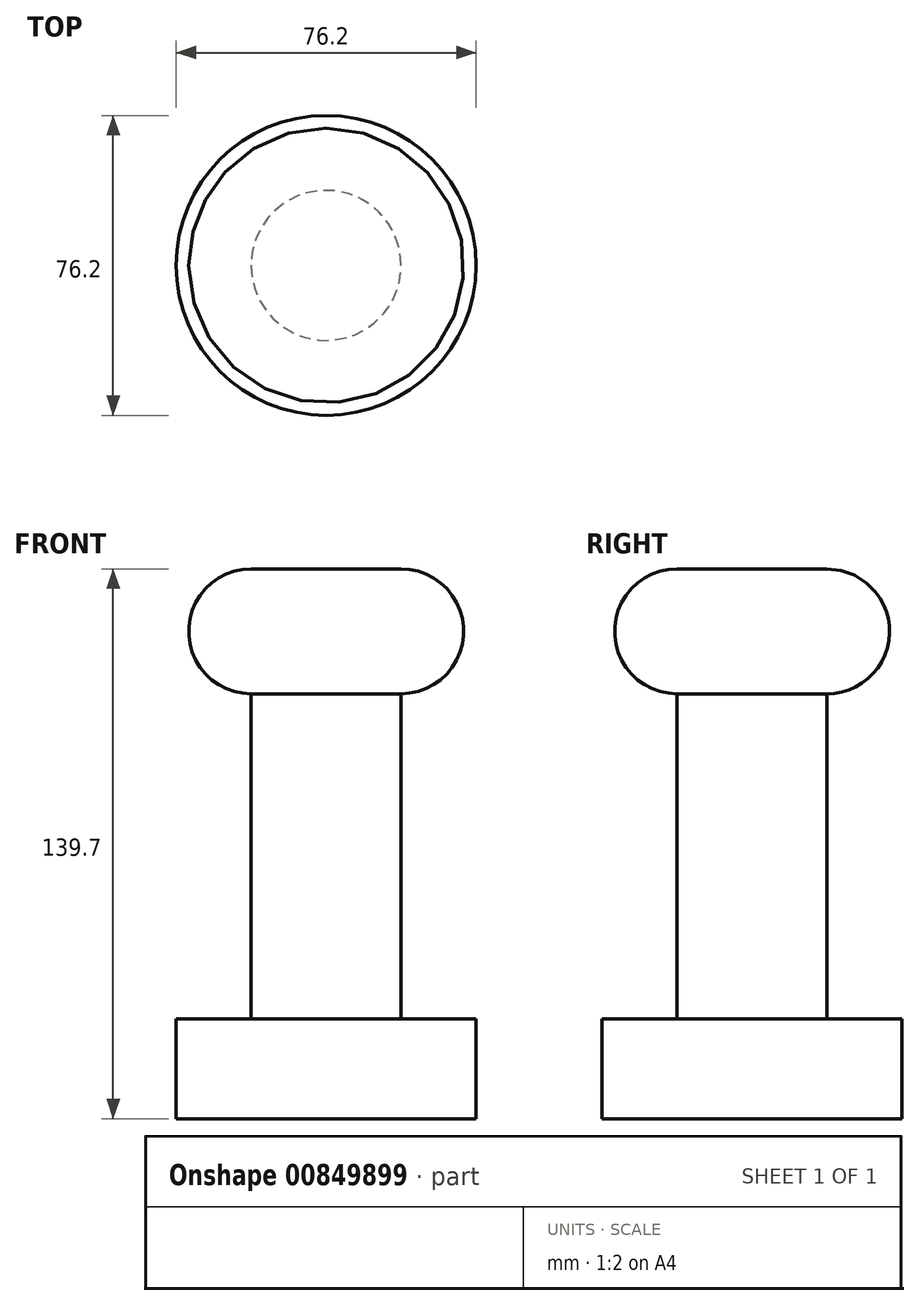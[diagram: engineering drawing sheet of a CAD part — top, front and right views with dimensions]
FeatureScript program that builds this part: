
annotation { "Feature Type Name" : "Feature", "Feature Type Description" : "" }
export const myFeature = defineFeature(function(context is Context, id is Id, definition is map)
    precondition{}
    {
        {
            var Q0;
            Q0=qCreatedBy(makeId("Front.planeOp"),FACE);
            var sketch = newSketch(context, id + "F0", { "sketchPlane" : qUnion([Q0])});
            skLineSegment(sketch, "E0", {"start": v(0, 0) * mm, "end": v(0, 139.7) * mm});
            skLineSegment(sketch, "E1", {"start": v(0, 0) * mm, "end": v(38.1, 0) * mm});
            skLineSegment(sketch, "E2", {"start": v(38.1, 0) * mm, "end": v(38.1, 25.4) * mm});
            skLineSegment(sketch, "E3", {"start": v(38.1, 25.4) * mm, "end": v(19.05, 25.4) * mm});
            skLineSegment(sketch, "E4", {"start": v(19.05, 25.4) * mm, "end": v(19.05, 107.95) * mm});
            skLineSegment(sketch, "E5", {"start": v(19.05, 107.95) * mm, "end": v(19.05, 139.7) * mm});
            skLineSegment(sketch, "E6", {"start": v(0, 139.7) * mm, "end": v(19.05, 139.7) * mm});
            skArc(sketch, "E7", {"start": v(19.05, 107.95) * mm, "mid": v(34.92, 123.83) * mm, "end": v(19.05, 139.7) * mm});
            skLineSegment(sketch, "E8", {"start": v(0, 0) * mm, "end": v(0, 165.1) * mm});
            skSolve(sketch);
        }
        {
            var Q0;
            {var subQ0=sQuery(id+"F0.wireOp",EDGE,"E1");Q0=makeQuery(id+"F0.imprint","IMPRINT",FACE,{"disambiguationData":[TD([[makeQuery(id+"F0.imprint","IMPRINT",EDGE,{"derivedFrom":subQ0}),1.0]])]});}
            var Q1;
            Q1=makeQuery(id+"F0.imprint","IMPRINT",FACE,{"disambiguationData":[TD([[makeQuery(id+"F0.imprint","IMPRINT",EDGE,{"derivedFrom":sQuery(id+"F0.wireOp",EDGE,"E5")}),-1.0]])]});
            var Q2;
            Q2=sQuery(id+"F0.wireOp",EDGE,"E8");
            revolve(context, id + "F1", {"surfaceOperationType" : NewSurfaceOperationType.NEW, "entities" : qUnion([Q0, Q1]), "axis" : qUnion([Q2]), "revolveType" : RevolveType.FULL});
        }
    });
